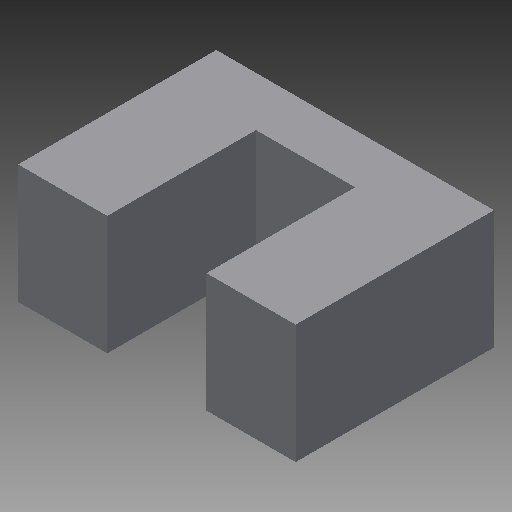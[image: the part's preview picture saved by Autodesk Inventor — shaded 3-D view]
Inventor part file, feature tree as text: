
AUTODESK INVENTOR PART (.ipt)
format: ipt  version: 2017 (Build 210142000, 142)  size: 86,528 bytes
history: native  units: in
note: dims shown in document units (in); Inventor stores cm internally (conversion verified against a paired STEP export)
features: other x3, sketch x2
ambient origin geometry x8: Origin, YZ Plane, XZ Plane, XY Plane, X Axis, Y Axis, Z Axis, Center Point
bodies: Solid1 (feature_tree)
feature tree (5):
  other  "opto_MIR4.ipt"
  other  "Solid1::opto_MIR4.ipt"
  other  "TaggingFeature1"
  sketch  "Sketch1"  dims[d0=0.3937in]
  sketch  "Sketch2"
